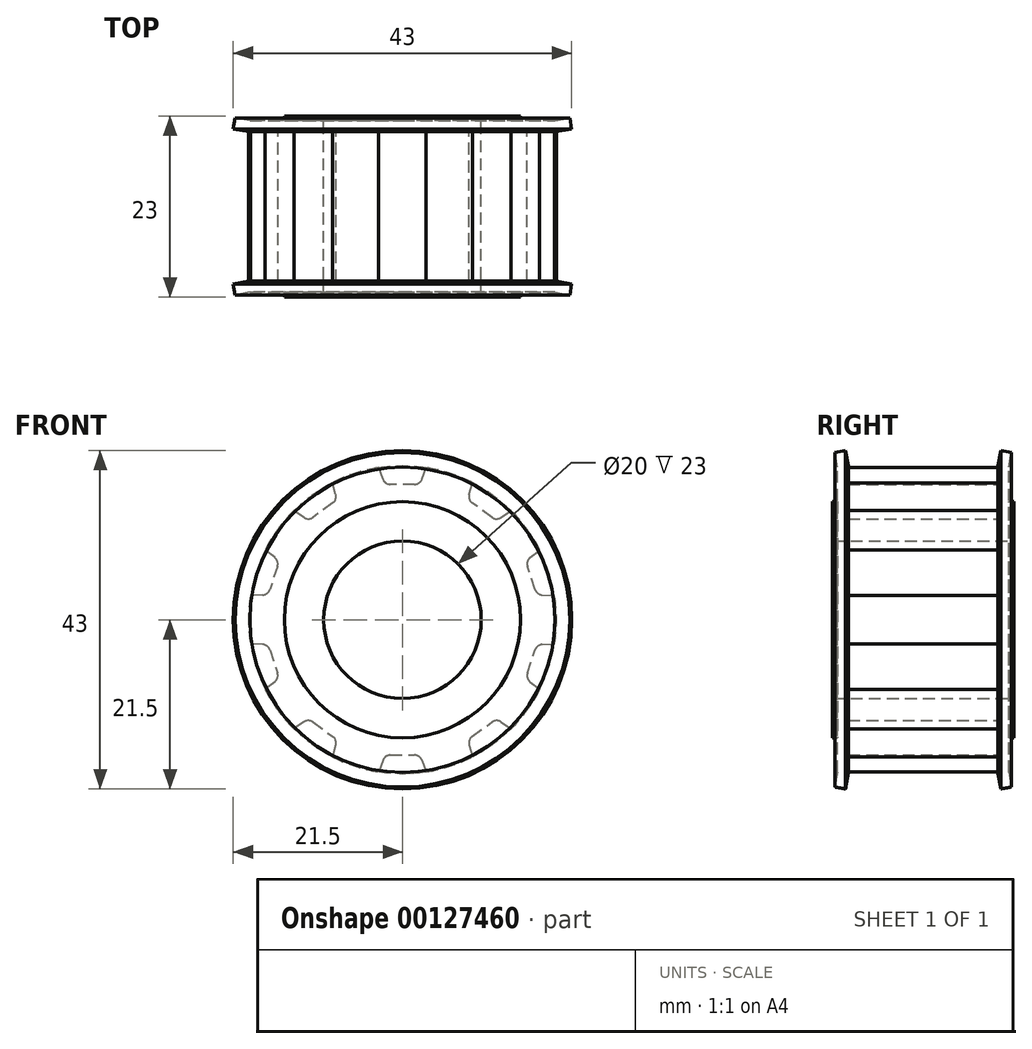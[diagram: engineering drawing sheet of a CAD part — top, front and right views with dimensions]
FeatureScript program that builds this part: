
annotation { "Feature Type Name" : "Feature", "Feature Type Description" : "" }
export const myFeature = defineFeature(function(context is Context, id is Id, definition is map)
    precondition{}
    {
        {
            var Q0;
            Q0=qCreatedBy(makeId("Front.planeOp"),FACE);
            var sketch = newSketch(context, id + "F0", { "sketchPlane" : qUnion([Q0])});
            skCircle(sketch, "E0", {"center": v(0, 0) * mm, "radius": 19.55 * mm, "construction": true});
            skCircle(sketch, "E1", {"center": v(0, 0) * mm, "radius": 15 * mm, "construction": true});
            skCircle(sketch, "E2", {"center": v(0, 0) * mm, "radius": 10 * mm, "construction": true});
            skSolve(sketch);
        }
        {
            var Q0;
            Q0=qCreatedBy(makeId("Front.planeOp"),FACE);
            var sketch = newSketch(context, id + "F1", { "sketchPlane" : qUnion([Q0])});
            skLineSegment(sketch, "E3", {"start": v(1.55, 17.2) * mm, "end": v(-1.55, 17.2) * mm});
            skLineSegment(sketch, "E4", {"start": v(-2.49, 17.86) * mm, "end": v(-3.02, 19.32) * mm});
            skLineSegment(sketch, "E5", {"start": v(2.49, 17.86) * mm, "end": v(3.02, 19.32) * mm});
            skLineSegment(sketch, "E6", {"start": v(0, 0) * mm, "end": v(0, 25.93) * mm, "construction": true});
            skPoint(sketch, "E7.visualSharp", {"position": v(2.25, 17.2) * mm});
            skArc(sketch, "E7.filletArc", {"start": v(1.55, 17.2) * mm, "mid": v(2.12, 17.38) * mm, "end": v(2.49, 17.86) * mm});
            skPoint(sketch, "E8.visualSharp", {"position": v(-2.25, 17.2) * mm});
            skArc(sketch, "E8.filletArc", {"start": v(-2.49, 17.86) * mm, "mid": v(-2.12, 17.38) * mm, "end": v(-1.55, 17.2) * mm});
            skArc(sketch, "E9.0", {"start": v(8.9, 17.4) * mm, "mid": v(6.04, 18.6) * mm, "end": v(3.02, 19.32) * mm});
            skLineSegment(sketch, "E10.1.0", {"start": v(-8.48, 15.91) * mm, "end": v(-8.9, 17.4) * mm});
            skArc(sketch, "E10.1.1", {"start": v(-8.86, 14.83) * mm, "mid": v(-8.5, 15.3) * mm, "end": v(-8.48, 15.91) * mm});
            skLineSegment(sketch, "E10.1.2", {"start": v(-8.86, 14.83) * mm, "end": v(-11.36, 13) * mm});
            skArc(sketch, "E10.1.3", {"start": v(-12.51, 12.98) * mm, "mid": v(-11.93, 12.81) * mm, "end": v(-11.36, 13) * mm});
            skLineSegment(sketch, "E10.1.4", {"start": v(-12.51, 12.98) * mm, "end": v(-13.8, 13.85) * mm});
            skLineSegment(sketch, "E10.2.0", {"start": v(-16.21, 7.89) * mm, "end": v(-17.44, 8.84) * mm});
            skArc(sketch, "E10.2.1", {"start": v(-15.88, 6.79) * mm, "mid": v(-15.87, 7.4) * mm, "end": v(-16.21, 7.89) * mm});
            skLineSegment(sketch, "E10.2.2", {"start": v(-15.88, 6.79) * mm, "end": v(-16.84, 3.84) * mm});
            skArc(sketch, "E10.2.3", {"start": v(-17.75, 3.15) * mm, "mid": v(-17.19, 3.35) * mm, "end": v(-16.84, 3.84) * mm});
            skLineSegment(sketch, "E10.2.4", {"start": v(-17.75, 3.15) * mm, "end": v(-19.3, 3.1) * mm});
            skLineSegment(sketch, "E10.3.0", {"start": v(-17.75, -3.15) * mm, "end": v(-19.3, -3.1) * mm});
            skArc(sketch, "E10.3.1", {"start": v(-16.84, -3.84) * mm, "mid": v(-17.19, -3.35) * mm, "end": v(-17.75, -3.15) * mm});
            skLineSegment(sketch, "E10.3.2", {"start": v(-16.84, -3.84) * mm, "end": v(-15.88, -6.79) * mm});
            skArc(sketch, "E10.3.3", {"start": v(-16.21, -7.89) * mm, "mid": v(-15.87, -7.4) * mm, "end": v(-15.88, -6.79) * mm});
            skLineSegment(sketch, "E10.3.4", {"start": v(-16.21, -7.89) * mm, "end": v(-17.44, -8.84) * mm});
            skLineSegment(sketch, "E10.4.0", {"start": v(-12.51, -12.98) * mm, "end": v(-13.8, -13.85) * mm});
            skArc(sketch, "E10.4.1", {"start": v(-11.36, -13) * mm, "mid": v(-11.93, -12.81) * mm, "end": v(-12.51, -12.98) * mm});
            skLineSegment(sketch, "E10.4.2", {"start": v(-11.36, -13) * mm, "end": v(-8.86, -14.83) * mm});
            skArc(sketch, "E10.4.3", {"start": v(-8.48, -15.91) * mm, "mid": v(-8.5, -15.3) * mm, "end": v(-8.86, -14.83) * mm});
            skLineSegment(sketch, "E10.4.4", {"start": v(-8.48, -15.91) * mm, "end": v(-8.9, -17.4) * mm});
            skLineSegment(sketch, "E10.5.0", {"start": v(-2.49, -17.86) * mm, "end": v(-3.02, -19.32) * mm});
            skArc(sketch, "E10.5.1", {"start": v(-1.55, -17.2) * mm, "mid": v(-2.12, -17.38) * mm, "end": v(-2.49, -17.86) * mm});
            skLineSegment(sketch, "E10.5.2", {"start": v(-1.55, -17.2) * mm, "end": v(1.55, -17.2) * mm});
            skArc(sketch, "E10.5.3", {"start": v(2.49, -17.86) * mm, "mid": v(2.12, -17.38) * mm, "end": v(1.55, -17.2) * mm});
            skLineSegment(sketch, "E10.5.4", {"start": v(2.49, -17.86) * mm, "end": v(3.02, -19.32) * mm});
            skLineSegment(sketch, "E10.6.0", {"start": v(8.48, -15.91) * mm, "end": v(8.9, -17.4) * mm});
            skArc(sketch, "E10.6.1", {"start": v(8.86, -14.83) * mm, "mid": v(8.5, -15.3) * mm, "end": v(8.48, -15.91) * mm});
            skLineSegment(sketch, "E10.6.2", {"start": v(8.86, -14.83) * mm, "end": v(11.36, -13) * mm});
            skArc(sketch, "E10.6.3", {"start": v(12.51, -12.98) * mm, "mid": v(11.93, -12.81) * mm, "end": v(11.36, -13) * mm});
            skLineSegment(sketch, "E10.6.4", {"start": v(12.51, -12.98) * mm, "end": v(13.8, -13.85) * mm});
            skLineSegment(sketch, "E10.7.0", {"start": v(16.21, -7.89) * mm, "end": v(17.44, -8.84) * mm});
            skArc(sketch, "E10.7.1", {"start": v(15.88, -6.79) * mm, "mid": v(15.87, -7.4) * mm, "end": v(16.21, -7.89) * mm});
            skLineSegment(sketch, "E10.7.2", {"start": v(15.88, -6.79) * mm, "end": v(16.84, -3.84) * mm});
            skArc(sketch, "E10.7.3", {"start": v(17.75, -3.15) * mm, "mid": v(17.19, -3.35) * mm, "end": v(16.84, -3.84) * mm});
            skLineSegment(sketch, "E10.7.4", {"start": v(17.75, -3.15) * mm, "end": v(19.3, -3.1) * mm});
            skLineSegment(sketch, "E10.8.0", {"start": v(17.75, 3.15) * mm, "end": v(19.3, 3.1) * mm});
            skArc(sketch, "E10.8.1", {"start": v(16.84, 3.84) * mm, "mid": v(17.19, 3.35) * mm, "end": v(17.75, 3.15) * mm});
            skLineSegment(sketch, "E10.8.2", {"start": v(16.84, 3.84) * mm, "end": v(15.88, 6.79) * mm});
            skArc(sketch, "E10.8.3", {"start": v(16.21, 7.89) * mm, "mid": v(15.87, 7.4) * mm, "end": v(15.88, 6.79) * mm});
            skLineSegment(sketch, "E10.8.4", {"start": v(16.21, 7.89) * mm, "end": v(17.44, 8.84) * mm});
            skLineSegment(sketch, "E10.9.0", {"start": v(12.51, 12.98) * mm, "end": v(13.8, 13.85) * mm});
            skArc(sketch, "E10.9.1", {"start": v(11.36, 13) * mm, "mid": v(11.93, 12.81) * mm, "end": v(12.51, 12.98) * mm});
            skLineSegment(sketch, "E10.9.2", {"start": v(11.36, 13) * mm, "end": v(8.86, 14.83) * mm});
            skArc(sketch, "E10.9.3", {"start": v(8.48, 15.91) * mm, "mid": v(8.5, 15.3) * mm, "end": v(8.86, 14.83) * mm});
            skLineSegment(sketch, "E10.9.4", {"start": v(8.48, 15.91) * mm, "end": v(8.9, 17.4) * mm});
            skArc(sketch, "E11.trimOffspring", {"start": v(17.44, 8.84) * mm, "mid": v(15.82, 11.5) * mm, "end": v(13.8, 13.85) * mm});
            skArc(sketch, "E12.trimOffspring", {"start": v(19.3, -3.1) * mm, "mid": v(19.55, 0) * mm, "end": v(19.3, 3.1) * mm});
            skArc(sketch, "E13.trimOffspring", {"start": v(13.8, -13.85) * mm, "mid": v(15.82, -11.5) * mm, "end": v(17.44, -8.84) * mm});
            skArc(sketch, "E14.trimOffspring", {"start": v(3.02, -19.32) * mm, "mid": v(6.04, -18.6) * mm, "end": v(8.9, -17.4) * mm});
            skArc(sketch, "E15.trimOffspring", {"start": v(-8.9, -17.4) * mm, "mid": v(-6.04, -18.6) * mm, "end": v(-3.02, -19.32) * mm});
            skArc(sketch, "E16.trimOffspring", {"start": v(-17.44, -8.84) * mm, "mid": v(-15.82, -11.5) * mm, "end": v(-13.8, -13.85) * mm});
            skArc(sketch, "E17.trimOffspring", {"start": v(-19.3, 3.1) * mm, "mid": v(-19.55, 0) * mm, "end": v(-19.3, -3.1) * mm});
            skArc(sketch, "E18.trimOffspring", {"start": v(-13.8, 13.85) * mm, "mid": v(-15.82, 11.5) * mm, "end": v(-17.44, 8.84) * mm});
            skArc(sketch, "E19.trimOffspring", {"start": v(-3.02, 19.32) * mm, "mid": v(-6.04, 18.6) * mm, "end": v(-8.9, 17.4) * mm});
            skSolve(sketch);
        }
        {
            var Q0;
            Q0=qSketchRegion(id+"F1",true);
            extrude(context, id + "F2", {"entities" : qUnion([Q0]), "endBound" : BoundingType.SYMMETRIC, "depth" : 19 * mm});
        }
        {
            var Q0;
            Q0=makeQuery(id+"F2.opExtrude","CAP_FACE",FACE,{"disambiguationData":[OSD([sQuery(id+"F1.wireOp",EDGE,"E3"),sQuery(id+"F1.wireOp",EDGE,"E4"),sQuery(id+"F1.wireOp",EDGE,"E5"),sQuery(id+"F1.wireOp",EDGE,"E7.filletArc"),sQuery(id+"F1.wireOp",EDGE,"E8.filletArc"),sQuery(id+"F1.wireOp",EDGE,"E9.0"),sQuery(id+"F1.wireOp",EDGE,"E10.1.0"),sQuery(id+"F1.wireOp",EDGE,"E10.1.1"),sQuery(id+"F1.wireOp",EDGE,"E10.1.2"),sQuery(id+"F1.wireOp",EDGE,"E10.1.3"),sQuery(id+"F1.wireOp",EDGE,"E10.1.4"),sQuery(id+"F1.wireOp",EDGE,"E10.2.0"),sQuery(id+"F1.wireOp",EDGE,"E10.2.1"),sQuery(id+"F1.wireOp",EDGE,"E10.2.2"),sQuery(id+"F1.wireOp",EDGE,"E10.2.3"),sQuery(id+"F1.wireOp",EDGE,"E10.2.4"),sQuery(id+"F1.wireOp",EDGE,"E10.3.0"),sQuery(id+"F1.wireOp",EDGE,"E10.3.1"),sQuery(id+"F1.wireOp",EDGE,"E10.3.2"),sQuery(id+"F1.wireOp",EDGE,"E10.3.3"),sQuery(id+"F1.wireOp",EDGE,"E10.3.4"),sQuery(id+"F1.wireOp",EDGE,"E10.4.0"),sQuery(id+"F1.wireOp",EDGE,"E10.4.1"),sQuery(id+"F1.wireOp",EDGE,"E10.4.2"),sQuery(id+"F1.wireOp",EDGE,"E10.4.3"),sQuery(id+"F1.wireOp",EDGE,"E10.4.4"),sQuery(id+"F1.wireOp",EDGE,"E10.5.0"),sQuery(id+"F1.wireOp",EDGE,"E10.5.1"),sQuery(id+"F1.wireOp",EDGE,"E10.5.2"),sQuery(id+"F1.wireOp",EDGE,"E10.5.3"),sQuery(id+"F1.wireOp",EDGE,"E10.5.4"),sQuery(id+"F1.wireOp",EDGE,"E10.6.0"),sQuery(id+"F1.wireOp",EDGE,"E10.6.1"),sQuery(id+"F1.wireOp",EDGE,"E10.6.2"),sQuery(id+"F1.wireOp",EDGE,"E10.6.3"),sQuery(id+"F1.wireOp",EDGE,"E10.6.4"),sQuery(id+"F1.wireOp",EDGE,"E10.7.0"),sQuery(id+"F1.wireOp",EDGE,"E10.7.1"),sQuery(id+"F1.wireOp",EDGE,"E10.7.2"),sQuery(id+"F1.wireOp",EDGE,"E10.7.3"),sQuery(id+"F1.wireOp",EDGE,"E10.7.4"),sQuery(id+"F1.wireOp",EDGE,"E10.8.0"),sQuery(id+"F1.wireOp",EDGE,"E10.8.1"),sQuery(id+"F1.wireOp",EDGE,"E10.8.2"),sQuery(id+"F1.wireOp",EDGE,"E10.8.3"),sQuery(id+"F1.wireOp",EDGE,"E10.8.4"),sQuery(id+"F1.wireOp",EDGE,"E10.9.0"),sQuery(id+"F1.wireOp",EDGE,"E10.9.1"),sQuery(id+"F1.wireOp",EDGE,"E10.9.2"),sQuery(id+"F1.wireOp",EDGE,"E10.9.3"),sQuery(id+"F1.wireOp",EDGE,"E10.9.4"),sQuery(id+"F1.wireOp",EDGE,"E11.trimOffspring"),sQuery(id+"F1.wireOp",EDGE,"E12.trimOffspring"),sQuery(id+"F1.wireOp",EDGE,"E13.trimOffspring"),sQuery(id+"F1.wireOp",EDGE,"E14.trimOffspring"),sQuery(id+"F1.wireOp",EDGE,"E15.trimOffspring"),sQuery(id+"F1.wireOp",EDGE,"E16.trimOffspring"),sQuery(id+"F1.wireOp",EDGE,"E17.trimOffspring"),sQuery(id+"F1.wireOp",EDGE,"E18.trimOffspring"),sQuery(id+"F1.wireOp",EDGE,"E19.trimOffspring")])],"isStart":false});
            var sketch = newSketch(context, id + "F3", { "sketchPlane" : qUnion([Q0])});
            skCircle(sketch, "E20.0", {"center": v(0, 0) * mm, "radius": 15 * mm});
            skSolve(sketch);
        }
        {
            var Q0;
            Q0=qSketchRegion(id+"F3",true);
            extrude(context, id + "F4", {"entities" : qUnion([Q0]), "operationType" : NewBodyOperationType.ADD, "depth" : 2 * mm});
        }
        {
            var Q0;
            Q0=makeQuery(id+"F2.opExtrude","CAP_FACE",FACE,{"disambiguationData":[OSD([sQuery(id+"F1.wireOp",EDGE,"E3"),sQuery(id+"F1.wireOp",EDGE,"E4"),sQuery(id+"F1.wireOp",EDGE,"E5"),sQuery(id+"F1.wireOp",EDGE,"E7.filletArc"),sQuery(id+"F1.wireOp",EDGE,"E8.filletArc"),sQuery(id+"F1.wireOp",EDGE,"E9.0"),sQuery(id+"F1.wireOp",EDGE,"E10.1.0"),sQuery(id+"F1.wireOp",EDGE,"E10.1.1"),sQuery(id+"F1.wireOp",EDGE,"E10.1.2"),sQuery(id+"F1.wireOp",EDGE,"E10.1.3"),sQuery(id+"F1.wireOp",EDGE,"E10.1.4"),sQuery(id+"F1.wireOp",EDGE,"E10.2.0"),sQuery(id+"F1.wireOp",EDGE,"E10.2.1"),sQuery(id+"F1.wireOp",EDGE,"E10.2.2"),sQuery(id+"F1.wireOp",EDGE,"E10.2.3"),sQuery(id+"F1.wireOp",EDGE,"E10.2.4"),sQuery(id+"F1.wireOp",EDGE,"E10.3.0"),sQuery(id+"F1.wireOp",EDGE,"E10.3.1"),sQuery(id+"F1.wireOp",EDGE,"E10.3.2"),sQuery(id+"F1.wireOp",EDGE,"E10.3.3"),sQuery(id+"F1.wireOp",EDGE,"E10.3.4"),sQuery(id+"F1.wireOp",EDGE,"E10.4.0"),sQuery(id+"F1.wireOp",EDGE,"E10.4.1"),sQuery(id+"F1.wireOp",EDGE,"E10.4.2"),sQuery(id+"F1.wireOp",EDGE,"E10.4.3"),sQuery(id+"F1.wireOp",EDGE,"E10.4.4"),sQuery(id+"F1.wireOp",EDGE,"E10.5.0"),sQuery(id+"F1.wireOp",EDGE,"E10.5.1"),sQuery(id+"F1.wireOp",EDGE,"E10.5.2"),sQuery(id+"F1.wireOp",EDGE,"E10.5.3"),sQuery(id+"F1.wireOp",EDGE,"E10.5.4"),sQuery(id+"F1.wireOp",EDGE,"E10.6.0"),sQuery(id+"F1.wireOp",EDGE,"E10.6.1"),sQuery(id+"F1.wireOp",EDGE,"E10.6.2"),sQuery(id+"F1.wireOp",EDGE,"E10.6.3"),sQuery(id+"F1.wireOp",EDGE,"E10.6.4"),sQuery(id+"F1.wireOp",EDGE,"E10.7.0"),sQuery(id+"F1.wireOp",EDGE,"E10.7.1"),sQuery(id+"F1.wireOp",EDGE,"E10.7.2"),sQuery(id+"F1.wireOp",EDGE,"E10.7.3"),sQuery(id+"F1.wireOp",EDGE,"E10.7.4"),sQuery(id+"F1.wireOp",EDGE,"E10.8.0"),sQuery(id+"F1.wireOp",EDGE,"E10.8.1"),sQuery(id+"F1.wireOp",EDGE,"E10.8.2"),sQuery(id+"F1.wireOp",EDGE,"E10.8.3"),sQuery(id+"F1.wireOp",EDGE,"E10.8.4"),sQuery(id+"F1.wireOp",EDGE,"E10.9.0"),sQuery(id+"F1.wireOp",EDGE,"E10.9.1"),sQuery(id+"F1.wireOp",EDGE,"E10.9.2"),sQuery(id+"F1.wireOp",EDGE,"E10.9.3"),sQuery(id+"F1.wireOp",EDGE,"E10.9.4"),sQuery(id+"F1.wireOp",EDGE,"E11.trimOffspring"),sQuery(id+"F1.wireOp",EDGE,"E12.trimOffspring"),sQuery(id+"F1.wireOp",EDGE,"E13.trimOffspring"),sQuery(id+"F1.wireOp",EDGE,"E14.trimOffspring"),sQuery(id+"F1.wireOp",EDGE,"E15.trimOffspring"),sQuery(id+"F1.wireOp",EDGE,"E16.trimOffspring"),sQuery(id+"F1.wireOp",EDGE,"E17.trimOffspring"),sQuery(id+"F1.wireOp",EDGE,"E18.trimOffspring"),sQuery(id+"F1.wireOp",EDGE,"E19.trimOffspring")])],"isStart":true});
            var sketch = newSketch(context, id + "F5", { "sketchPlane" : qUnion([Q0])});
            skCircle(sketch, "E21.0", {"center": v(0, 0) * mm, "radius": 15 * mm});
            skSolve(sketch);
        }
        {
            var Q0;
            Q0=qSketchRegion(id+"F5",true);
            extrude(context, id + "F6", {"entities" : qUnion([Q0]), "operationType" : NewBodyOperationType.ADD, "depth" : 2 * mm});
        }
        {
            var Q0;
            Q0=makeQuery(id+"F6.opExtrude","CAP_FACE",FACE,{"disambiguationData":[OSD([sQuery(id+"F5.wireOp",EDGE,"E21.0")])],"isStart":false});
            var sketch = newSketch(context, id + "F7", { "sketchPlane" : qUnion([Q0])});
            skCircle(sketch, "E22.0", {"center": v(0, 0) * mm, "radius": 10 * mm});
            skSolve(sketch);
        }
        {
            var Q0;
            Q0=qSketchRegion(id+"F7",true);
            extrude(context, id + "F8", {"entities" : qUnion([Q0]), "operationType" : NewBodyOperationType.REMOVE, "oppositeDirection" : true, "depth" : 25 * mm});
        }
        {
            var Q0;
            Q0=qCreatedBy(makeId("Right.planeOp"),FACE);
            var sketch = newSketch(context, id + "F9", { "sketchPlane" : qUnion([Q0])});
            skLineSegment(sketch, "E23", {"start": v(-10.9, -15) * mm, "end": v(-9.5, -15) * mm});
            skLineSegment(sketch, "E24", {"start": v(-9.5, -15) * mm, "end": v(-9.5, -19.5) * mm});
            skLineSegment(sketch, "E25", {"start": v(-9.5, -19.5) * mm, "end": v(-9.85, -21.5) * mm});
            skLineSegment(sketch, "E26", {"start": v(-9.85, -21.5) * mm, "end": v(-11.23, -21.26) * mm});
            skLineSegment(sketch, "E27", {"start": v(-11.23, -21.26) * mm, "end": v(-10.9, -19.38) * mm});
            skLineSegment(sketch, "E28", {"start": v(-10.9, -19.38) * mm, "end": v(-10.9, -15) * mm});
            skLineSegment(sketch, "E29.0.MirrorCS", {"start": v(10.9, -19.38) * mm, "end": v(10.9, -15) * mm});
            skLineSegment(sketch, "E30.0.MirrorCS", {"start": v(10.9, -15) * mm, "end": v(9.5, -15) * mm});
            skLineSegment(sketch, "E31.0.MirrorCS", {"start": v(9.5, -15) * mm, "end": v(9.5, -19.5) * mm});
            skLineSegment(sketch, "E32.0.MirrorCS", {"start": v(9.5, -19.5) * mm, "end": v(9.85, -21.5) * mm});
            skLineSegment(sketch, "E33.0.MirrorCS", {"start": v(11.23, -21.26) * mm, "end": v(10.9, -19.38) * mm});
            skLineSegment(sketch, "E34.0.MirrorCS", {"start": v(9.85, -21.5) * mm, "end": v(11.23, -21.26) * mm});
            skLineSegment(sketch, "E35", {"start": v(0, 0) * mm, "end": v(18.13, 0) * mm, "construction": true});
            skSolve(sketch);
        }
        {
            var Q0;
            Q0=qSketchRegion(id+"F9",true);
            var Q1;
            Q1=sQuery(id+"F9.wireOp",EDGE,"E35");
            revolve(context, id + "F10", {"operationType" : NewBodyOperationType.ADD, "entities" : qUnion([Q0]), "axis" : qUnion([Q1]), "revolveType" : RevolveType.FULL});
        }
    });
